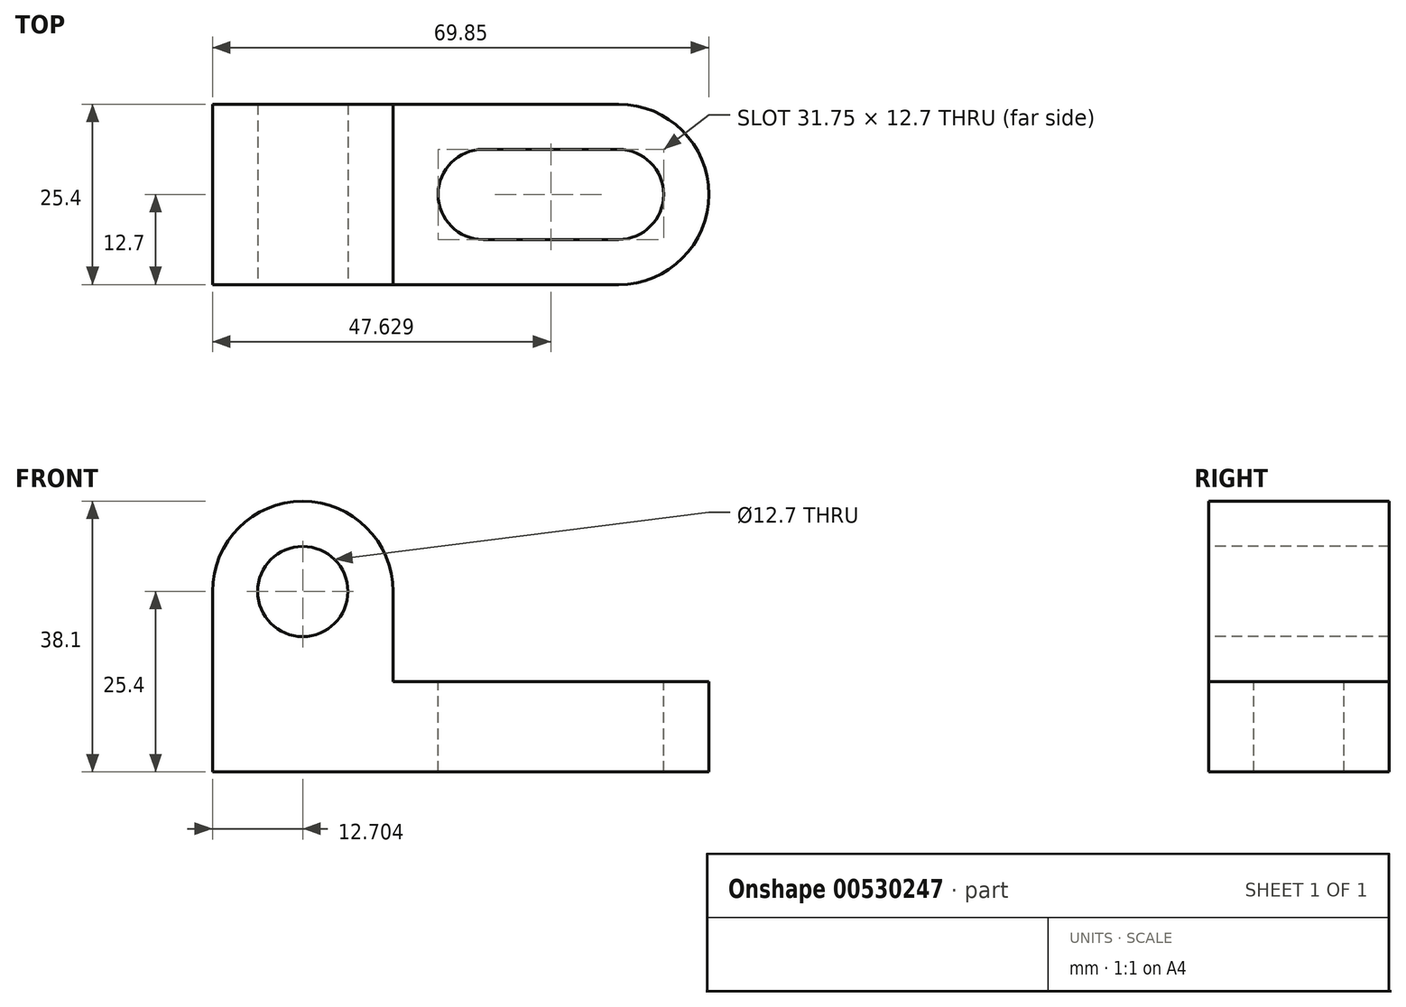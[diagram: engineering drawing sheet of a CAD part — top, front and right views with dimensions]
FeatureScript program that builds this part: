
annotation { "Feature Type Name" : "Feature", "Feature Type Description" : "" }
export const myFeature = defineFeature(function(context is Context, id is Id, definition is map)
    precondition{}
    {
        {
            var Q0;
            Q0=qCreatedBy(makeId("Front.planeOp"),FACE);
            var sketch = newSketch(context, id + "F0", { "sketchPlane" : qUnion([Q0])});
            skLineSegment(sketch, "E0", {"start": v(-70, 0) * mm, "end": v(-12.85, 0) * mm});
            skLineSegment(sketch, "E1", {"start": v(-12.85, 0) * mm, "end": v(-12.85, 12.7) * mm});
            skLineSegment(sketch, "E2", {"start": v(-12.85, 12.7) * mm, "end": v(-44.6, 12.7) * mm});
            skLineSegment(sketch, "E3", {"start": v(-44.6, 12.7) * mm, "end": v(-44.6, 25.4) * mm});
            skLineSegment(sketch, "E4", {"start": v(-44.6, 25.4) * mm, "end": v(-70, 25.4) * mm});
            skLineSegment(sketch, "E5", {"start": v(-70, 25.4) * mm, "end": v(-70, 0) * mm});
            skArc(sketch, "E6", {"start": v(-44.6, 25.4) * mm, "mid": v(-57.3, 38.1) * mm, "end": v(-70, 25.4) * mm});
            skSolve(sketch);
        }
        {
            var Q0;
            Q0 = qSketchRegion(id + "F0", true);
            extrude(context, id + "F1", {"entities" : qUnion([Q0]), "depth" : 25.4 * mm, "offsetDistance" : 25.4 * mm});
        }
        {
            var Q0;
            Q0=makeQuery(id+"F1.opExtrude","SWEPT_FACE",FACE,{"disambiguationData":[OSD([sQuery(id+"F0.wireOp",EDGE,"E2")])]});
            var sketch = newSketch(context, id + "F2", { "sketchPlane" : qUnion([Q0])});
            skArc(sketch, "E7", {"start": v(-12.85, -25.4) * mm, "mid": v(-0.15, -12.7) * mm, "end": v(-12.85, 0) * mm});
            skSolve(sketch);
        }
        {
            var Q0;
            Q0=makeQuery(id+"F2.imprint","IMPRINT",FACE,{"disambiguationData":[TD([[makeQuery(id+"F2.imprint","IMPRINT",EDGE,{"derivedFrom":sQuery(id+"F2.wireOp",EDGE,"E7")}),1.0]])]});
            extrude(context, id + "F3", {"entities" : qUnion([Q0]), "operationType" : NewBodyOperationType.ADD, "oppositeDirection" : true, "depth" : 12.7 * mm, "offsetDistance" : 25.4 * mm});
        }
        {
            var Q0;
            {var subQ0=sQuery(id+"F0.wireOp",EDGE,"E2");Q0=makeQuery(id+"F3.boolean.opBoolean","MERGE",FACE,{"derivedFrom":[makeQuery(id+"F1.opExtrude","SWEPT_FACE",FACE,{"disambiguationData":[OSD([subQ0])]}),makeQuery(id+"F3.opExtrude","CAP_FACE",FACE,{"disambiguationData":[OSD([sQuery(id+"F0.wireOp",EDGE,"E1"),subQ0,sQuery(id+"F2.wireOp",EDGE,"E7")])],"isStart":true})]});}
            var sketch = newSketch(context, id + "F4", { "sketchPlane" : qUnion([Q0])});
            skLineSegment(sketch, "E8", {"start": v(-12.85, -12.7) * mm, "end": v(-12.85, -6.35) * mm});
            skLineSegment(sketch, "E9", {"start": v(-12.85, -6.35) * mm, "end": v(-31.9, -6.35) * mm});
            skLineSegment(sketch, "E10", {"start": v(-31.9, -6.35) * mm, "end": v(-31.9, -19.05) * mm});
            skLineSegment(sketch, "E11", {"start": v(-31.9, -19.05) * mm, "end": v(-12.85, -19.05) * mm});
            skLineSegment(sketch, "E12", {"start": v(-12.85, -19.05) * mm, "end": v(-12.85, -12.7) * mm});
            skArc(sketch, "E13", {"start": v(-12.85, -19.05) * mm, "mid": v(-6.5, -12.7) * mm, "end": v(-12.85, -6.35) * mm});
            skArc(sketch, "E14", {"start": v(-31.9, -6.35) * mm, "mid": v(-38.25, -12.7) * mm, "end": v(-31.9, -19.05) * mm});
            skSolve(sketch);
        }
        {
            var Q0;
            Q0 = qSketchRegion(id + "F4", true);
            extrude(context, id + "F5", {"entities" : qUnion([Q0]), "operationType" : NewBodyOperationType.REMOVE, "oppositeDirection" : true, "depth" : 25.4 * mm, "offsetDistance" : 25.4 * mm});
        }
        {
            var Q0;
            Q0=makeQuery(id+"F1.opExtrude","CAP_FACE",FACE,{"disambiguationData":[OSD([sQuery(id+"F0.wireOp",EDGE,"E0"),sQuery(id+"F0.wireOp",EDGE,"E1"),sQuery(id+"F0.wireOp",EDGE,"E2"),sQuery(id+"F0.wireOp",EDGE,"E3"),sQuery(id+"F0.wireOp",EDGE,"E5"),sQuery(id+"F0.wireOp",EDGE,"E6")])],"isStart":false});
            var sketch = newSketch(context, id + "F6", { "sketchPlane" : qUnion([Q0])});
            skCircle(sketch, "E15", {"center": v(-57.3, 25.4) * mm, "radius": 6.35 * mm});
            skSolve(sketch);
        }
        {
            var Q0;
            Q0=makeQuery(id+"F6.imprint","IMPRINT",FACE,{"disambiguationData":[TD([[makeQuery(id+"F6.imprint","IMPRINT",EDGE,{"derivedFrom":sQuery(id+"F6.wireOp",EDGE,"E15")}),1.0]])]});
            extrude(context, id + "F7", {"entities" : qUnion([Q0]), "operationType" : NewBodyOperationType.REMOVE, "oppositeDirection" : true, "depth" : 25.4 * mm, "offsetDistance" : 25.4 * mm});
        }
    });
